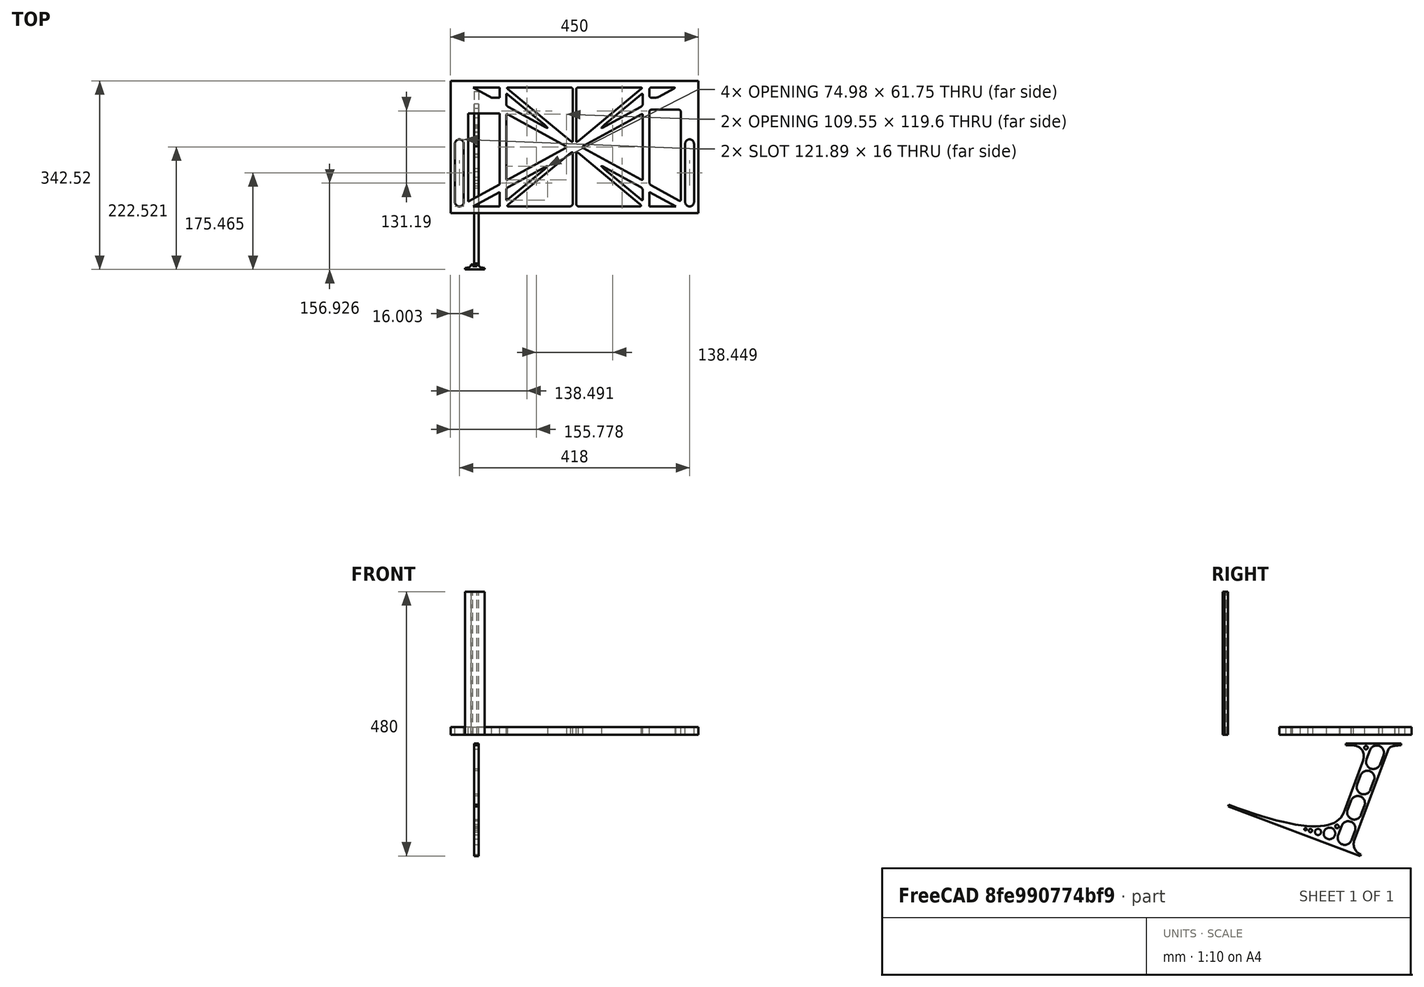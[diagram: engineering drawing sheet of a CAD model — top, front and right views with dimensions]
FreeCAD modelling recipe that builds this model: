
FCSTD DOCUMENT  (FreeCAD 0.19R0.19.2)
Label: laptopStand108
License: All rights reserved
LicenseURL: http://en.wikipedia.org/wiki/All_rights_reserved
objects: Sketcher::SketchObject×3, Part::Extrusion×3
note: 6 computed .brp shape members not serialized (recipe doc carries the construction recipe); baked Part::Feature solids carry a one-line shape summary decoded from their .brp

FEATURE [Sketcher::SketchObject] Sketch
  FullyConstrained = false
  sketch-geometry (298):
    g0: LineSegment StartX=-10.9272 StartY=-82.7794 StartZ=0 EndX=46.0728 EndY=-51.4823 EndZ=0
    g1: LineSegment StartX=366.073 StartY=-91.7794 StartZ=0 EndX=318.073 EndY=-65.424 EndZ=0
    g2: LineSegment StartX=-10.9272 StartY=77.3346 StartZ=0 EndX=-10.9272 EndY=-82.7794 EndZ=0
    g3: LineSegment StartX=-1.92719 StartY=-91.7794 StartZ=0 EndX=46.0728 EndY=-91.7794 EndZ=0
    g4: LineSegment StartX=318.073 StartY=-65.424 StartZ=0 EndX=318.073 EndY=-91.7794 EndZ=0
    g5: LineSegment StartX=318.073 StartY=-91.7794 StartZ=0 EndX=366.073 EndY=-91.7794 EndZ=0
    g6: LineSegment StartX=46.0728 StartY=-65.424 StartZ=0 EndX=-1.92719 EndY=-91.7794 EndZ=0
    g7: LineSegment StartX=46.0728 StartY=-65.424 StartZ=0 EndX=46.0728 EndY=-91.7794 EndZ=0
    g8: LineSegment StartX=46.0728 StartY=77.3346 StartZ=0 EndX=46.0728 EndY=-51.4823 EndZ=0
    g9: LineSegment StartX=-42.9272 StartY=136.221 StartZ=0 EndX=-42.9272 EndY=-103.779 EndZ=0
    g10: LineSegment StartX=407.073 StartY=136.221 StartZ=0 EndX=407.073 EndY=-103.779 EndZ=0
    g11: ArcOfCircle CenterX=-26.9272 CenterY=22.1087 CenterZ=0 NormalX=0 NormalY=0 NormalZ=1 AngleXU=0 Radius=8 StartAngle=1e-16 EndAngle=3.14159
    g12: ArcOfCircle CenterX=-26.9272 CenterY=-83.7794 CenterZ=0 NormalX=0 NormalY=0 NormalZ=1 AngleXU=0 Radius=8 StartAngle=3.14159 EndAngle=6.28319
    g13: LineSegment StartX=-34.9272 StartY=22.1087 StartZ=0 EndX=-34.9272 EndY=-83.7794 EndZ=0
    g14: LineSegment StartX=-18.9272 StartY=22.1087 StartZ=0 EndX=-18.9272 EndY=-83.7794 EndZ=0
    g15: ArcOfCircle CenterX=391.073 CenterY=22.1087 CenterZ=0 NormalX=0 NormalY=0 NormalZ=1 AngleXU=0 Radius=8 StartAngle=-4.4e-15 EndAngle=3.14159
    g16: LineSegment StartX=399.073 StartY=22.1087 StartZ=0 EndX=399.073 EndY=-83.7794 EndZ=0
    g17: LineSegment StartX=383.073 StartY=22.1087 StartZ=0 EndX=383.073 EndY=-83.7794 EndZ=0
    g18: ArcOfCircle CenterX=391.073 CenterY=-83.7794 CenterZ=0 NormalX=0 NormalY=0 NormalZ=1 AngleXU=0 Radius=8 StartAngle=3.14159 EndAngle=6.28319
    g19: Circle CenterX=175.022 CenterY=27.0628 CenterZ=0 NormalX=0 NormalY=0 NormalZ=1 AngleXU=0 Radius=1
    g20: Circle CenterX=179.022 CenterY=24.8665 CenterZ=0 NormalX=0 NormalY=0 NormalZ=1 AngleXU=0 Radius=1
    g21: Circle CenterX=179.022 CenterY=27.0628 CenterZ=0 NormalX=0 NormalY=0 NormalZ=1 AngleXU=0 Radius=1
    g22: BSplineCurve PolesCount=3 KnotsCount=2 Degree=2 IsPeriodic=0
    g23: GeomPoint X=175.022 Y=27.0628 Z=0
    g24: GeomPoint X=179.022 Y=27.0628 Z=0
    g25: Circle CenterX=189.124 CenterY=27.0628 CenterZ=0 NormalX=0 NormalY=0 NormalZ=1 AngleXU=0 Radius=1
    g26: Circle CenterX=185.124 CenterY=24.8665 CenterZ=0 NormalX=0 NormalY=0 NormalZ=1 AngleXU=0 Radius=1
    g27: Circle CenterX=185.124 CenterY=27.0628 CenterZ=0 NormalX=0 NormalY=0 NormalZ=1 AngleXU=0 Radius=1
    g28: BSplineCurve PolesCount=3 KnotsCount=2 Degree=2 IsPeriodic=0
    g29: GeomPoint X=189.124 Y=27.0628 Z=0
    g30: GeomPoint X=185.124 Y=27.0628 Z=0
    g31: Circle CenterX=175.022 CenterY=5.37834 CenterZ=0 NormalX=0 NormalY=0 NormalZ=1 AngleXU=0 Radius=1
    g32: Circle CenterX=179.022 CenterY=7.57463 CenterZ=0 NormalX=0 NormalY=0 NormalZ=1 AngleXU=0 Radius=1
    g33: Circle CenterX=179.022 CenterY=5.34704 CenterZ=0 NormalX=0 NormalY=0 NormalZ=1 AngleXU=0 Radius=1
    g34: BSplineCurve PolesCount=3 KnotsCount=2 Degree=2 IsPeriodic=0
    g35: GeomPoint X=175.022 Y=5.37834 Z=0
    g36: GeomPoint X=179.022 Y=5.34704 Z=0
    g37: Circle CenterX=189.124 CenterY=5.37834 CenterZ=0 NormalX=0 NormalY=0 NormalZ=1 AngleXU=0 Radius=1
    g38: Circle CenterX=185.124 CenterY=7.57463 CenterZ=0 NormalX=0 NormalY=0 NormalZ=1 AngleXU=0 Radius=1
    g39: Circle CenterX=185.124 CenterY=5.34704 CenterZ=0 NormalX=0 NormalY=0 NormalZ=1 AngleXU=0 Radius=1
    g40: BSplineCurve PolesCount=3 KnotsCount=2 Degree=2 IsPeriodic=0
    g41: GeomPoint X=189.124 Y=5.37834 Z=0
    g42: GeomPoint X=185.124 Y=5.34704 Z=0
    g43: Circle CenterX=165.871 CenterY=18.1458 CenterZ=0 NormalX=0 NormalY=0 NormalZ=1 AngleXU=0 Radius=1
    g44: Circle CenterX=169.377 CenterY=16.2206 CenterZ=0 NormalX=0 NormalY=0 NormalZ=1 AngleXU=0 Radius=1
    g45: Circle CenterX=165.871 CenterY=14.2954 CenterZ=0 NormalX=0 NormalY=0 NormalZ=1 AngleXU=0 Radius=1
    g46: BSplineCurve PolesCount=3 KnotsCount=2 Degree=2 IsPeriodic=0
    g47: GeomPoint X=165.871 Y=18.1458 Z=0
    g48: GeomPoint X=165.871 Y=14.2954 Z=0
    g49: Circle CenterX=198.275 CenterY=18.1458 CenterZ=0 NormalX=0 NormalY=0 NormalZ=1 AngleXU=0 Radius=1
    g50: Circle CenterX=194.768 CenterY=16.2206 CenterZ=0 NormalX=0 NormalY=0 NormalZ=1 AngleXU=0 Radius=1
    g51: Circle CenterX=198.275 CenterY=14.2954 CenterZ=0 NormalX=0 NormalY=0 NormalZ=1 AngleXU=0 Radius=1
    g52: BSplineCurve PolesCount=3 KnotsCount=2 Degree=2 IsPeriodic=0
    g53: GeomPoint X=198.275 Y=18.1458 Z=0
    g54: GeomPoint X=198.275 Y=14.2954 Z=0
    g55: LineSegment StartX=407.073 StartY=-103.779 StartZ=0 EndX=-42.9272 EndY=-103.779 EndZ=0
    g56: LineSegment StartX=407.073 StartY=136.221 StartZ=0 EndX=-42.9272 EndY=136.221 EndZ=0
    g57: LineSegment StartX=46.0728 StartY=77.3346 StartZ=0 EndX=-10.9272 EndY=77.3346 EndZ=0
    g58: LineSegment StartX=46.0728 StartY=105.865 StartZ=0 EndX=31.5028 EndY=105.865 EndZ=0
    g59: LineSegment StartX=46.0728 StartY=124.221 StartZ=0 EndX=46.0728 EndY=105.865 EndZ=0
    g60: LineSegment StartX=-1.92719 StartY=124.221 StartZ=0 EndX=31.5028 EndY=105.865 EndZ=0
    g61: LineSegment StartX=46.0728 StartY=124.221 StartZ=0 EndX=-1.92719 EndY=124.221 EndZ=0
    g62: Circle CenterX=125.607 CenterY=54.1951 CenterZ=0 NormalX=0 NormalY=0 NormalZ=1 AngleXU=0 Radius=1
    g63: Circle CenterX=139.632 CenterY=46.4944 CenterZ=0 NormalX=0 NormalY=0 NormalZ=1 AngleXU=0 Radius=1
    g64: Circle CenterX=127.326 CenterY=56.7187 CenterZ=0 NormalX=0 NormalY=0 NormalZ=1 AngleXU=0 Radius=1
    g65: BSplineCurve PolesCount=3 KnotsCount=2 Degree=2 IsPeriodic=0
    g66: GeomPoint X=125.607 Y=54.1951 Z=0
    g67: GeomPoint X=127.326 Y=56.7187 Z=0
    g68: Circle CenterX=236.821 CenterY=56.7187 CenterZ=0 NormalX=0 NormalY=0 NormalZ=1 AngleXU=0 Radius=1
    g69: Circle CenterX=224.513 CenterY=46.4944 CenterZ=0 NormalX=0 NormalY=0 NormalZ=1 AngleXU=0 Radius=1
    g70: Circle CenterX=238.538 CenterY=54.1951 CenterZ=0 NormalX=0 NormalY=0 NormalZ=1 AngleXU=0 Radius=1
    g71: BSplineCurve PolesCount=3 KnotsCount=2 Degree=2 IsPeriodic=0
    g72: GeomPoint X=236.821 Y=56.7187 Z=0
    g73: GeomPoint X=238.538 Y=54.1951 Z=0
    g74: Circle CenterX=238.538 CenterY=-21.7539 CenterZ=0 NormalX=0 NormalY=0 NormalZ=1 AngleXU=0 Radius=1
    g75: Circle CenterX=224.513 CenterY=-14.0532 CenterZ=0 NormalX=0 NormalY=0 NormalZ=1 AngleXU=0 Radius=1
    g76: Circle CenterX=236.821 CenterY=-24.2775 CenterZ=0 NormalX=0 NormalY=0 NormalZ=1 AngleXU=0 Radius=1
    g77: BSplineCurve PolesCount=3 KnotsCount=2 Degree=2 IsPeriodic=0
    g78: GeomPoint X=238.538 Y=-21.7539 Z=0
    g79: GeomPoint X=236.821 Y=-24.2775 Z=0
    g80: Circle CenterX=125.607 CenterY=-21.7539 CenterZ=0 NormalX=0 NormalY=0 NormalZ=1 AngleXU=0 Radius=1
    g81: Circle CenterX=139.632 CenterY=-14.0532 CenterZ=0 NormalX=0 NormalY=0 NormalZ=1 AngleXU=0 Radius=1
    g82: Circle CenterX=127.325 CenterY=-24.2775 CenterZ=0 NormalX=0 NormalY=0 NormalZ=1 AngleXU=0 Radius=1
    g83: BSplineCurve PolesCount=3 KnotsCount=2 Degree=2 IsPeriodic=0
    g84: GeomPoint X=125.607 Y=-21.7539 Z=0
    g85: GeomPoint X=127.325 Y=-24.2775 Z=0
    g86: Circle CenterX=302.996 CenterY=111.695 CenterZ=0 NormalX=0 NormalY=0 NormalZ=1 AngleXU=0 Radius=1
    g87: Circle CenterX=306.073 CenterY=114.251 CenterZ=0 NormalX=0 NormalY=0 NormalZ=1 AngleXU=0 Radius=1
    g88: Circle CenterX=306.073 CenterY=110.251 CenterZ=0 NormalX=0 NormalY=0 NormalZ=1 AngleXU=0 Radius=1
    g89: BSplineCurve PolesCount=3 KnotsCount=2 Degree=2 IsPeriodic=0
    g90: GeomPoint X=302.996 Y=111.695 Z=0
    g91: GeomPoint X=306.073 Y=110.251 Z=0
    g92: Circle CenterX=306.073 CenterY=95.2763 CenterZ=0 NormalX=0 NormalY=0 NormalZ=1 AngleXU=0 Radius=1
    g93: Circle CenterX=306.073 CenterY=91.2763 CenterZ=0 NormalX=0 NormalY=0 NormalZ=1 AngleXU=0 Radius=1
    g94: Circle CenterX=302.567 CenterY=89.3511 CenterZ=0 NormalX=0 NormalY=0 NormalZ=1 AngleXU=0 Radius=1
    g95: BSplineCurve PolesCount=3 KnotsCount=2 Degree=2 IsPeriodic=0
    g96: GeomPoint X=306.073 Y=95.2763 Z=0
    g97: GeomPoint X=302.567 Y=89.3511 Z=0
    g98: LineSegment StartX=306.073 StartY=110.251 StartZ=0 EndX=306.073 EndY=95.2763 EndZ=0
    g99: LineSegment StartX=302.996 StartY=111.695 StartZ=0 EndX=236.821 EndY=56.7187 EndZ=0
    g100: LineSegment StartX=238.538 StartY=54.1951 StartZ=0 EndX=302.567 EndY=89.3511 EndZ=0
    g101: Circle CenterX=61.1496 CenterY=111.695 CenterZ=0 NormalX=0 NormalY=0 NormalZ=1 AngleXU=0 Radius=1
    g102: Circle CenterX=58.0728 CenterY=114.251 CenterZ=0 NormalX=0 NormalY=0 NormalZ=1 AngleXU=0 Radius=1
    g103: Circle CenterX=58.0728 CenterY=110.251 CenterZ=0 NormalX=0 NormalY=0 NormalZ=1 AngleXU=0 Radius=1
    g104: BSplineCurve PolesCount=3 KnotsCount=2 Degree=2 IsPeriodic=0
    g105: GeomPoint X=61.1496 Y=111.695 Z=0
    g106: GeomPoint X=58.0728 Y=110.251 Z=0
    g107: Circle CenterX=61.5791 CenterY=89.3511 CenterZ=0 NormalX=0 NormalY=0 NormalZ=1 AngleXU=0 Radius=1
    g108: Circle CenterX=58.0728 CenterY=91.2763 CenterZ=0 NormalX=0 NormalY=0 NormalZ=1 AngleXU=0 Radius=1
    g109: Circle CenterX=58.0728 CenterY=95.2763 CenterZ=0 NormalX=0 NormalY=0 NormalZ=1 AngleXU=0 Radius=1
    g110: BSplineCurve PolesCount=3 KnotsCount=2 Degree=2 IsPeriodic=0
    g111: GeomPoint X=61.5791 Y=89.3511 Z=0
    g112: GeomPoint X=58.0728 Y=95.2763 Z=0
    g113: LineSegment StartX=58.0728 StartY=110.251 StartZ=0 EndX=58.0728 EndY=95.2763 EndZ=0
    g114: LineSegment StartX=61.1496 StartY=111.695 StartZ=0 EndX=127.326 EndY=56.7187 EndZ=0
    g115: LineSegment StartX=125.607 StartY=54.1951 StartZ=0 EndX=61.5791 EndY=89.3511 EndZ=0
    g116: Circle CenterX=61.5791 CenterY=-56.9099 CenterZ=0 NormalX=0 NormalY=0 NormalZ=1 AngleXU=0 Radius=1
    g117: Circle CenterX=58.0728 CenterY=-58.8351 CenterZ=0 NormalX=0 NormalY=0 NormalZ=1 AngleXU=0 Radius=1
    g118: Circle CenterX=58.0728 CenterY=-62.8351 CenterZ=0 NormalX=0 NormalY=0 NormalZ=1 AngleXU=0 Radius=1
    g119: BSplineCurve PolesCount=3 KnotsCount=2 Degree=2 IsPeriodic=0
    g120: GeomPoint X=61.5791 Y=-56.9099 Z=0
    g121: GeomPoint X=58.0728 Y=-62.8351 Z=0
    g122: Circle CenterX=58.0728 CenterY=-77.8102 CenterZ=0 NormalX=0 NormalY=0 NormalZ=1 AngleXU=0 Radius=1
    g123: Circle CenterX=58.0728 CenterY=-81.8102 CenterZ=0 NormalX=0 NormalY=0 NormalZ=1 AngleXU=0 Radius=1
    g124: Circle CenterX=61.1496 CenterY=-79.2541 CenterZ=0 NormalX=0 NormalY=0 NormalZ=1 AngleXU=0 Radius=1
    g125: BSplineCurve PolesCount=3 KnotsCount=2 Degree=2 IsPeriodic=0
    g126: GeomPoint X=58.0728 Y=-77.8102 Z=0
    g127: GeomPoint X=61.1496 Y=-79.2541 Z=0
    g128: LineSegment StartX=58.0728 StartY=-62.8351 StartZ=0 EndX=58.0728 EndY=-77.8102 EndZ=0
    g129: LineSegment StartX=61.1496 StartY=-79.2541 StartZ=0 EndX=127.325 EndY=-24.2775 EndZ=0
    g130: LineSegment StartX=125.607 StartY=-21.7539 StartZ=0 EndX=61.5791 EndY=-56.9099 EndZ=0
    g131: Circle CenterX=302.567 CenterY=-56.9099 CenterZ=0 NormalX=0 NormalY=0 NormalZ=1 AngleXU=0 Radius=1
    g132: Circle CenterX=306.073 CenterY=-58.8351 CenterZ=0 NormalX=0 NormalY=0 NormalZ=1 AngleXU=0 Radius=1
    g133: Circle CenterX=306.073 CenterY=-62.8351 CenterZ=0 NormalX=0 NormalY=0 NormalZ=1 AngleXU=0 Radius=1
    g134: BSplineCurve PolesCount=3 KnotsCount=2 Degree=2 IsPeriodic=0
    g135: GeomPoint X=302.567 Y=-56.9099 Z=0
    g136: GeomPoint X=306.073 Y=-62.8351 Z=0
    g137: Circle CenterX=302.996 CenterY=-79.2541 CenterZ=0 NormalX=0 NormalY=0 NormalZ=1 AngleXU=0 Radius=1
    g138: Circle CenterX=306.073 CenterY=-81.8102 CenterZ=0 NormalX=0 NormalY=0 NormalZ=1 AngleXU=0 Radius=1
    g139: Circle CenterX=306.073 CenterY=-77.8102 CenterZ=0 NormalX=0 NormalY=0 NormalZ=1 AngleXU=0 Radius=1
    g140: BSplineCurve PolesCount=3 KnotsCount=2 Degree=2 IsPeriodic=0
    g141: GeomPoint X=302.996 Y=-79.2541 Z=0
    g142: GeomPoint X=306.073 Y=-77.8102 Z=0
    g143: LineSegment StartX=306.073 StartY=-62.8351 StartZ=0 EndX=306.073 EndY=-77.8102 EndZ=0
    g144: LineSegment StartX=302.996 StartY=-79.2541 StartZ=0 EndX=236.821 EndY=-24.2775 EndZ=0
    g145: LineSegment StartX=238.538 StartY=-21.7539 StartZ=0 EndX=302.567 EndY=-56.9099 EndZ=0
    g146: Circle CenterX=61.6457 CenterY=-88.8112 CenterZ=0 NormalX=0 NormalY=0 NormalZ=1 AngleXU=0 Radius=1
    g147: Circle CenterX=58.0728 CenterY=-91.7794 CenterZ=0 NormalX=0 NormalY=0 NormalZ=1 AngleXU=0 Radius=1
    g148: Circle CenterX=63.9135 CenterY=-91.7794 CenterZ=0 NormalX=0 NormalY=0 NormalZ=1 AngleXU=0 Radius=1
    g149: BSplineCurve PolesCount=3 KnotsCount=2 Degree=2 IsPeriodic=0
    g150: GeomPoint X=61.6457 Y=-88.8112 Z=0
    g151: GeomPoint X=63.9135 Y=-91.7794 Z=0
    g152: Circle CenterX=179.022 CenterY=-85.8163 CenterZ=0 NormalX=0 NormalY=0 NormalZ=1 AngleXU=0 Radius=1
    g153: Circle CenterX=179.022 CenterY=-91.7794 CenterZ=0 NormalX=0 NormalY=0 NormalZ=1 AngleXU=0 Radius=1
    g154: Circle CenterX=171.895 CenterY=-91.7794 CenterZ=0 NormalX=0 NormalY=0 NormalZ=1 AngleXU=0 Radius=1
    g155: BSplineCurve PolesCount=3 KnotsCount=2 Degree=2 IsPeriodic=0
    g156: GeomPoint X=179.022 Y=-85.8163 Z=0
    g157: GeomPoint X=171.895 Y=-91.7794 Z=0
    g158: Circle CenterX=185.124 CenterY=-86.2028 CenterZ=0 NormalX=0 NormalY=0 NormalZ=1 AngleXU=0 Radius=1
    g159: Circle CenterX=185.124 CenterY=-91.7794 CenterZ=0 NormalX=0 NormalY=0 NormalZ=1 AngleXU=0 Radius=1
    g160: Circle CenterX=191.747 CenterY=-91.7794 CenterZ=0 NormalX=0 NormalY=0 NormalZ=1 AngleXU=0 Radius=1
    g161: BSplineCurve PolesCount=3 KnotsCount=2 Degree=2 IsPeriodic=0
    g162: GeomPoint X=185.124 Y=-86.2028 Z=0
    g163: GeomPoint X=191.747 Y=-91.7794 Z=0
    g164: Circle CenterX=299.888 CenterY=-86.6413 CenterZ=0 NormalX=0 NormalY=0 NormalZ=1 AngleXU=0 Radius=1
    g165: Circle CenterX=306.073 CenterY=-91.7794 CenterZ=0 NormalX=0 NormalY=0 NormalZ=1 AngleXU=0 Radius=1
    g166: Circle CenterX=298.776 CenterY=-91.7794 CenterZ=0 NormalX=0 NormalY=0 NormalZ=1 AngleXU=0 Radius=1
    g167: BSplineCurve PolesCount=3 KnotsCount=2 Degree=2 IsPeriodic=0
    g168: GeomPoint X=299.888 Y=-86.6413 Z=0
    g169: GeomPoint X=298.776 Y=-91.7794 Z=0
    g170: LineSegment StartX=189.124 StartY=5.37834 StartZ=0 EndX=299.888 EndY=-86.6413 EndZ=0
    g171: LineSegment StartX=298.776 StartY=-91.7794 StartZ=0 EndX=191.747 EndY=-91.7794 EndZ=0
    g172: LineSegment StartX=185.124 StartY=-86.2028 StartZ=0 EndX=185.124 EndY=5.34704 EndZ=0
    g173: LineSegment StartX=179.022 StartY=5.34704 StartZ=0 EndX=179.022 EndY=-85.8163 EndZ=0
    g174: LineSegment StartX=171.895 StartY=-91.7794 StartZ=0 EndX=63.9135 EndY=-91.7794 EndZ=0
    g175: LineSegment StartX=61.6457 StartY=-88.8112 StartZ=0 EndX=175.022 EndY=5.37834 EndZ=0
    g176: Circle CenterX=302.073 CenterY=124.221 CenterZ=0 NormalX=0 NormalY=0 NormalZ=1 AngleXU=0 Radius=1
    g177: Circle CenterX=306.073 CenterY=124.221 CenterZ=0 NormalX=0 NormalY=0 NormalZ=1 AngleXU=0 Radius=1
    g178: Circle CenterX=302.996 CenterY=121.665 CenterZ=0 NormalX=0 NormalY=0 NormalZ=1 AngleXU=0 Radius=1
    g179: BSplineCurve PolesCount=3 KnotsCount=2 Degree=2 IsPeriodic=0
    g180: GeomPoint X=302.073 Y=124.221 Z=0
    g181: GeomPoint X=302.996 Y=121.665 Z=0
    g182: Circle CenterX=189.124 CenterY=124.221 CenterZ=0 NormalX=0 NormalY=0 NormalZ=1 AngleXU=0 Radius=1
    g183: Circle CenterX=185.124 CenterY=124.221 CenterZ=0 NormalX=0 NormalY=0 NormalZ=1 AngleXU=0 Radius=1
    g184: Circle CenterX=185.124 CenterY=120.221 CenterZ=0 NormalX=0 NormalY=0 NormalZ=1 AngleXU=0 Radius=1
    g185: BSplineCurve PolesCount=3 KnotsCount=2 Degree=2 IsPeriodic=0
    g186: GeomPoint X=189.124 Y=124.221 Z=0
    g187: GeomPoint X=185.124 Y=120.221 Z=0
    g188: Circle CenterX=175.022 CenterY=124.221 CenterZ=0 NormalX=0 NormalY=0 NormalZ=1 AngleXU=0 Radius=1
    g189: Circle CenterX=179.022 CenterY=124.221 CenterZ=0 NormalX=0 NormalY=0 NormalZ=1 AngleXU=0 Radius=1
    g190: Circle CenterX=179.022 CenterY=120.221 CenterZ=0 NormalX=0 NormalY=0 NormalZ=1 AngleXU=0 Radius=1
    g191: BSplineCurve PolesCount=3 KnotsCount=2 Degree=2 IsPeriodic=0
    g192: GeomPoint X=175.022 Y=124.221 Z=0
    g193: GeomPoint X=179.022 Y=120.221 Z=0
    g194: Circle CenterX=62.0728 CenterY=124.221 CenterZ=0 NormalX=0 NormalY=0 NormalZ=1 AngleXU=0 Radius=1
    g195: Circle CenterX=58.0728 CenterY=124.221 CenterZ=0 NormalX=0 NormalY=0 NormalZ=1 AngleXU=0 Radius=1
    g196: Circle CenterX=61.1496 CenterY=121.665 CenterZ=0 NormalX=0 NormalY=0 NormalZ=1 AngleXU=0 Radius=1
    g197: BSplineCurve PolesCount=3 KnotsCount=2 Degree=2 IsPeriodic=0
    g198: GeomPoint X=62.0728 Y=124.221 Z=0
    g199: GeomPoint X=61.1496 Y=121.665 Z=0
    g200: LineSegment StartX=62.0728 StartY=124.221 StartZ=0 EndX=175.022 EndY=124.221 EndZ=0
    g201: LineSegment StartX=179.022 StartY=120.221 StartZ=0 EndX=179.022 EndY=27.0628 EndZ=0
    g202: LineSegment StartX=185.124 StartY=27.0628 StartZ=0 EndX=185.124 EndY=120.221 EndZ=0
    g203: LineSegment StartX=189.124 StartY=124.221 StartZ=0 EndX=302.073 EndY=124.221 EndZ=0
    g204: LineSegment StartX=302.996 StartY=121.665 StartZ=0 EndX=189.124 EndY=27.0628 EndZ=0
    g205: LineSegment StartX=175.022 StartY=27.0628 StartZ=0 EndX=61.1496 EndY=121.665 EndZ=0
    g206: Circle CenterX=61.5791 CenterY=75.4095 CenterZ=0 NormalX=0 NormalY=0 NormalZ=1 AngleXU=0 Radius=1
    g207: Circle CenterX=58.0728 CenterY=77.3346 CenterZ=0 NormalX=0 NormalY=0 NormalZ=1 AngleXU=0 Radius=1
    g208: Circle CenterX=58.0728 CenterY=73.3346 CenterZ=0 NormalX=0 NormalY=0 NormalZ=1 AngleXU=0 Radius=1
    g209: BSplineCurve PolesCount=3 KnotsCount=2 Degree=2 IsPeriodic=0
    g210: GeomPoint X=61.5791 Y=75.4095 Z=0
    g211: GeomPoint X=58.0728 Y=73.3346 Z=0
    g212: Circle CenterX=58.0728 CenterY=-40.8935 CenterZ=0 NormalX=0 NormalY=0 NormalZ=1 AngleXU=0 Radius=1
    g213: Circle CenterX=58.0728 CenterY=-44.8935 CenterZ=0 NormalX=0 NormalY=0 NormalZ=1 AngleXU=0 Radius=1
    g214: Circle CenterX=61.5791 CenterY=-42.9683 CenterZ=0 NormalX=0 NormalY=0 NormalZ=1 AngleXU=0 Radius=1
    g215: BSplineCurve PolesCount=3 KnotsCount=2 Degree=2 IsPeriodic=0
    g216: GeomPoint X=58.0728 Y=-40.8935 Z=0
    g217: GeomPoint X=61.5791 Y=-42.9683 Z=0
    g218: LineSegment StartX=61.5791 StartY=-42.9683 StartZ=0 EndX=165.871 EndY=14.2954 EndZ=0
    g219: LineSegment StartX=165.871 StartY=18.1458 StartZ=0 EndX=61.5791 EndY=75.4095 EndZ=0
    g220: LineSegment StartX=58.0728 StartY=73.3346 StartZ=0 EndX=58.0728 EndY=-40.8935 EndZ=0
    g221: Circle CenterX=302.567 CenterY=-42.9683 CenterZ=0 NormalX=0 NormalY=0 NormalZ=1 AngleXU=0 Radius=1
    g222: Circle CenterX=306.073 CenterY=-44.8935 CenterZ=0 NormalX=0 NormalY=0 NormalZ=1 AngleXU=0 Radius=1
    g223: Circle CenterX=306.073 CenterY=-40.8935 CenterZ=0 NormalX=0 NormalY=0 NormalZ=1 AngleXU=0 Radius=1
    g224: BSplineCurve PolesCount=3 KnotsCount=2 Degree=2 IsPeriodic=0
    g225: GeomPoint X=302.567 Y=-42.9683 Z=0
    g226: GeomPoint X=306.073 Y=-40.8935 Z=0
    g227: Circle CenterX=306.073 CenterY=73.3346 CenterZ=0 NormalX=0 NormalY=0 NormalZ=1 AngleXU=0 Radius=1
    g228: Circle CenterX=306.073 CenterY=77.3346 CenterZ=0 NormalX=0 NormalY=0 NormalZ=1 AngleXU=0 Radius=1
    g229: Circle CenterX=302.567 CenterY=75.4095 CenterZ=0 NormalX=0 NormalY=0 NormalZ=1 AngleXU=0 Radius=1
    g230: BSplineCurve PolesCount=3 KnotsCount=2 Degree=2 IsPeriodic=0
    g231: GeomPoint X=306.073 Y=73.3346 Z=0
    g232: GeomPoint X=302.567 Y=75.4095 Z=0
    g233: LineSegment StartX=302.567 StartY=-42.9683 StartZ=0 EndX=198.275 EndY=14.2954 EndZ=0
    g234: LineSegment StartX=198.275 StartY=18.1458 StartZ=0 EndX=302.567 EndY=75.4095 EndZ=0
    g235: LineSegment StartX=306.073 StartY=73.3346 StartZ=0 EndX=306.073 EndY=-40.8935 EndZ=0
    g236: LineSegment StartX=322.073 StartY=105.865 StartZ=0 EndX=328.643 EndY=105.865 EndZ=0
    g237: LineSegment StartX=318.073 StartY=120.221 StartZ=0 EndX=318.073 EndY=109.865 EndZ=0
    g238: LineSegment StartX=336.157 StartY=107.779 StartZ=0 EndX=362.567 EndY=122.294 EndZ=0
    g239: Circle CenterX=362.073 CenterY=124.221 CenterZ=0 NormalX=0 NormalY=0 NormalZ=1 AngleXU=0 Radius=1
    g240: Circle CenterX=366.073 CenterY=124.221 CenterZ=0 NormalX=0 NormalY=0 NormalZ=1 AngleXU=0 Radius=1
    g241: Circle CenterX=362.567 CenterY=122.294 CenterZ=0 NormalX=0 NormalY=0 NormalZ=1 AngleXU=0 Radius=1
    g242: BSplineCurve PolesCount=3 KnotsCount=2 Degree=2 IsPeriodic=0
    g243: GeomPoint X=362.073 Y=124.221 Z=0
    g244: GeomPoint X=362.567 Y=122.294 Z=0
    g245: Circle CenterX=322.073 CenterY=124.221 CenterZ=0 NormalX=0 NormalY=0 NormalZ=1 AngleXU=0 Radius=1
    g246: Circle CenterX=318.073 CenterY=124.221 CenterZ=0 NormalX=0 NormalY=0 NormalZ=1 AngleXU=0 Radius=1
    g247: Circle CenterX=318.073 CenterY=120.221 CenterZ=0 NormalX=0 NormalY=0 NormalZ=1 AngleXU=0 Radius=1
    g248: BSplineCurve PolesCount=3 KnotsCount=2 Degree=2 IsPeriodic=0
    g249: GeomPoint X=322.073 Y=124.221 Z=0
    g250: GeomPoint X=318.073 Y=120.221 Z=0
    g251: Circle CenterX=322.073 CenterY=105.865 CenterZ=0 NormalX=0 NormalY=0 NormalZ=1 AngleXU=0 Radius=1
    g252: Circle CenterX=318.073 CenterY=105.865 CenterZ=0 NormalX=0 NormalY=0 NormalZ=1 AngleXU=0 Radius=1
    g253: Circle CenterX=318.073 CenterY=109.865 CenterZ=0 NormalX=0 NormalY=0 NormalZ=1 AngleXU=0 Radius=1
    g254: BSplineCurve PolesCount=3 KnotsCount=2 Degree=2 IsPeriodic=0
    g255: GeomPoint X=322.073 Y=105.865 Z=0
    g256: GeomPoint X=318.073 Y=109.865 Z=0
    g257: Circle CenterX=336.157 CenterY=107.779 CenterZ=0 NormalX=0 NormalY=0 NormalZ=1 AngleXU=0 Radius=1
    g258: Circle CenterX=332.651 CenterY=105.853 CenterZ=0 NormalX=0 NormalY=0 NormalZ=1 AngleXU=0 Radius=1
    g259: Circle CenterX=328.643 CenterY=105.865 CenterZ=0 NormalX=0 NormalY=0 NormalZ=1 AngleXU=0 Radius=1
    g260: BSplineCurve PolesCount=3 KnotsCount=2 Degree=2 IsPeriodic=0
    g261: GeomPoint X=336.157 Y=107.779 Z=0
    g262: GeomPoint X=328.643 Y=105.865 Z=0
    g263: LineSegment StartX=322.073 StartY=124.221 StartZ=0 EndX=362.073 EndY=124.221 EndZ=0
    g264: Circle CenterX=371.567 CenterY=-80.8644 CenterZ=0 NormalX=0 NormalY=0 NormalZ=1 AngleXU=0 Radius=1
    g265: Circle CenterX=375.073 CenterY=-82.7896 CenterZ=0 NormalX=0 NormalY=0 NormalZ=1 AngleXU=0 Radius=1
    g266: Circle CenterX=375.073 CenterY=-78.7896 CenterZ=0 NormalX=0 NormalY=0 NormalZ=1 AngleXU=0 Radius=1
    g267: BSplineCurve PolesCount=3 KnotsCount=2 Degree=2 IsPeriodic=0
    g268: GeomPoint X=371.567 Y=-80.8644 Z=0
    g269: GeomPoint X=375.073 Y=-78.7896 Z=0
    g270: Circle CenterX=321.579 CenterY=-53.4075 CenterZ=0 NormalX=0 NormalY=0 NormalZ=1 AngleXU=0 Radius=1
    g271: Circle CenterX=318.073 CenterY=-51.4823 CenterZ=0 NormalX=0 NormalY=0 NormalZ=1 AngleXU=0 Radius=1
    g272: Circle CenterX=318.073 CenterY=-47.4823 CenterZ=0 NormalX=0 NormalY=0 NormalZ=1 AngleXU=0 Radius=1
    g273: BSplineCurve PolesCount=3 KnotsCount=2 Degree=2 IsPeriodic=0
    g274: GeomPoint X=321.579 Y=-53.4075 Z=0
    g275: GeomPoint X=318.073 Y=-47.4823 Z=0
    g276: Circle CenterX=318.073 CenterY=79.9235 CenterZ=0 NormalX=0 NormalY=0 NormalZ=1 AngleXU=0 Radius=1
    g277: Circle CenterX=318.073 CenterY=83.9235 CenterZ=0 NormalX=0 NormalY=0 NormalZ=1 AngleXU=0 Radius=1
    g278: Circle CenterX=322.073 CenterY=83.9235 CenterZ=0 NormalX=0 NormalY=0 NormalZ=1 AngleXU=0 Radius=1
    g279: BSplineCurve PolesCount=3 KnotsCount=2 Degree=2 IsPeriodic=0
    g280: GeomPoint X=318.073 Y=79.9235 Z=0
    g281: GeomPoint X=322.073 Y=83.9235 Z=0
    g282: Circle CenterX=375.073 CenterY=79.9235 CenterZ=0 NormalX=0 NormalY=0 NormalZ=1 AngleXU=0 Radius=1
    g283: Circle CenterX=375.073 CenterY=83.9235 CenterZ=0 NormalX=0 NormalY=0 NormalZ=1 AngleXU=0 Radius=1
    g284: Circle CenterX=371.073 CenterY=83.9235 CenterZ=0 NormalX=0 NormalY=0 NormalZ=1 AngleXU=0 Radius=1
    g285: BSplineCurve PolesCount=3 KnotsCount=2 Degree=2 IsPeriodic=0
    g286: GeomPoint X=375.073 Y=79.9235 Z=0
    g287: GeomPoint X=371.073 Y=83.9235 Z=0
    g288: LineSegment StartX=322.073 StartY=83.9235 StartZ=0 EndX=371.073 EndY=83.9235 EndZ=0
    g289: LineSegment StartX=375.073 StartY=79.9235 StartZ=0 EndX=375.073 EndY=-78.7896 EndZ=0
    g290: LineSegment StartX=371.567 StartY=-80.8644 StartZ=0 EndX=321.579 EndY=-53.4075 EndZ=0
    g291: LineSegment StartX=318.073 StartY=-47.4823 StartZ=0 EndX=318.073 EndY=79.9235 EndZ=0
    g292: LineSegment StartX=319.639 StartY=-65.1825 StartZ=0 EndX=324.101 EndY=-67.6327 EndZ=0
    g293: LineSegment StartX=366.617 StartY=-91.048 StartZ=0 EndX=360.96 EndY=-87.9419 EndZ=0
    g294: LineSegment StartX=365.563 StartY=-92.7205 StartZ=0 EndX=358.36 EndY=-92.7205 EndZ=0
    g295: LineSegment StartX=318.76 StartY=-92.6854 StartZ=0 EndX=325.717 EndY=-92.6854 EndZ=0
    g296: LineSegment StartX=317.038 StartY=-91.4204 StartZ=0 EndX=317.038 EndY=-87.2391 EndZ=0
    g297: LineSegment StartX=317.566 StartY=-66.1569 StartZ=0 EndX=317.566 EndY=-69.2841 EndZ=0
  constraints (494):
    c: Horizontal(g3)
    c: Coincident(g4,g1)
    c: Coincident(g7,g6)
    c: Coincident(g0,g8)
    c: Block(g1)
    c: Block(g4)
    c: Block(g7)
    c: Block(g6)
    c: Block(g0)
    c: Block(g2)
    c: Block(g5)
    c: Block(g3)
    c: Vertical(g9)
    c: Vertical(g10)
    c: Block(g10)
    c: Block(g9)
    c: Tangent(g11,g14) = 1.5708
    c: Tangent(g11,g13) = -1.5708
    c: Tangent(g13,g12) = -1.5708
    c: Tangent(g14,g12) = 1.5708
    c: Vertical(g13)
    c: Equal(g11,g12)
    c: Block(g14)
    c: Block(g13)
    c: Tangent(g15,g16) = 1.5708
    c: Tangent(g16,g18) = 1.5708
    c: Equal(g15,g18)
    c: Coincident(g17,g15)
    c: Coincident(g17,g18)
    c: Block(g16)
    c: Block(g17)
    c: Weight(g19) = 1
    c: Equal(g19,g20)
    c: Equal(g19,g21)
    c: InternalAlignment(g19,g22)
    c: InternalAlignment(g20,g22)
    c: InternalAlignment(g21,g22)
    c: InternalAlignment(g23,g22)
    c: InternalAlignment(g24,g22)
    c: Weight(g25) = 1
    c: Equal(g25,g26)
    c: Equal(g25,g27)
    c: InternalAlignment(g25,g28)
    c: InternalAlignment(g26,g28)
    c: InternalAlignment(g27,g28)
    c: InternalAlignment(g29,g28)
    c: InternalAlignment(g30,g28)
    c: Block(g28)
    c: Block(g22)
    c: Weight(g31) = 1
    c: Equal(g31,g32)
    c: Equal(g31,g33)
    c: InternalAlignment(g31,g34)
    c: InternalAlignment(g32,g34)
    c: InternalAlignment(g33,g34)
    c: InternalAlignment(g35,g34)
    c: InternalAlignment(g36,g34)
    c: Weight(g37) = 1
    c: Equal(g37,g38)
    c: Equal(g37,g39)
    c: InternalAlignment(g37,g40)
    c: InternalAlignment(g38,g40)
    c: InternalAlignment(g39,g40)
    c: InternalAlignment(g41,g40)
    c: InternalAlignment(g42,g40)
    c: Block(g40)
    c: Block(g34)
    c: Weight(g43) = 1
    c: Equal(g43,g44)
    c: Equal(g43,g45)
    c: InternalAlignment(g43,g46)
    c: InternalAlignment(g44,g46)
    c: InternalAlignment(g45,g46)
    c: InternalAlignment(g47,g46)
    c: InternalAlignment(g48,g46)
    c: Weight(g49) = 1
    c: Equal(g49,g50)
    c: Equal(g49,g51)
    c: InternalAlignment(g49,g52)
    c: InternalAlignment(g50,g52)
    c: InternalAlignment(g51,g52)
    c: InternalAlignment(g53,g52)
    c: InternalAlignment(g54,g52)
    c: Block(g46)
    c: Block(g52)
    c: Coincident(g55,g10)
    c: Coincident(g55,g9)
    c: Horizontal(g55)
    c: Distance(g55) = 450
    c: Coincident(g56,g10)
    c: Coincident(g56,g9)
    c: Horizontal(g56)
    c: Horizontal(g57)
    c: Coincident(g8,g57)
    c: Horizontal(g58)
    c: Vertical(g59)
    c: Block(g59)
    c: Block(g58)
    c: Block(g57)
    c: Distance(g59) = 18.3554
    c: Coincident(g61,g59)
    c: Coincident(g61,g60)
    c: Horizontal(g61)
    c: Block(g61)
    c: Block(g60)
    c: Coincident(g58,g60)
    c: Coincident(g2,g57)
    c: Weight(g62) = 1
    c: Equal(g62,g63)
    c: Equal(g62,g64)
    c: InternalAlignment(g62,g65)
    c: InternalAlignment(g63,g65)
    c: InternalAlignment(g64,g65)
    c: InternalAlignment(g66,g65)
    c: InternalAlignment(g67,g65)
    c: Block(g65)
    c: Weight(g68) = 1
    c: Equal(g68,g69)
    c: Equal(g68,g70)
    c: InternalAlignment(g68,g71)
    c: InternalAlignment(g69,g71)
    c: InternalAlignment(g70,g71)
    c: InternalAlignment(g72,g71)
    c: InternalAlignment(g73,g71)
    c: Block(g71)
    c: Weight(g74) = 1
    c: Equal(g74,g75)
    c: Equal(g74,g76)
    c: InternalAlignment(g74,g77)
    c: InternalAlignment(g75,g77)
    c: InternalAlignment(g76,g77)
    c: InternalAlignment(g78,g77)
    c: InternalAlignment(g79,g77)
    c: Block(g77)
    c: Weight(g80) = 1
    c: Equal(g80,g81)
    c: Equal(g80,g82)
    c: InternalAlignment(g80,g83)
    c: InternalAlignment(g81,g83)
    c: InternalAlignment(g82,g83)
    c: InternalAlignment(g84,g83)
    c: InternalAlignment(g85,g83)
    c: Block(g83)
    c: Weight(g86) = 1
    c: Equal(g86,g87)
    c: Equal(g86,g88)
    c: InternalAlignment(g86,g89)
    c: InternalAlignment(g87,g89)
    c: InternalAlignment(g88,g89)
    c: InternalAlignment(g90,g89)
    c: InternalAlignment(g91,g89)
    c: Weight(g92) = 1
    c: Equal(g92,g93)
    c: Equal(g92,g94)
    c: InternalAlignment(g92,g95)
    c: InternalAlignment(g93,g95)
    c: InternalAlignment(g94,g95)
    c: InternalAlignment(g96,g95)
    c: InternalAlignment(g97,g95)
    c: Block(g89)
    c: Block(g95)
    c: Coincident(g98,g89)
    c: Coincident(g98,g95)
    c: Vertical(g98)
    c: Coincident(g99,g89)
    c: Coincident(g99,g71)
    c: Coincident(g100,g71)
    c: Coincident(g100,g95)
    c: Weight(g101) = 1
    c: Equal(g101,g102)
    c: Equal(g101,g103)
    c: InternalAlignment(g101,g104)
    c: InternalAlignment(g102,g104)
    c: InternalAlignment(g103,g104)
    c: InternalAlignment(g105,g104)
    c: InternalAlignment(g106,g104)
    c: Weight(g107) = 1
    c: Equal(g107,g108)
    c: Equal(g107,g109)
    c: InternalAlignment(g107,g110)
    c: InternalAlignment(g108,g110)
    c: InternalAlignment(g109,g110)
    c: InternalAlignment(g111,g110)
    c: InternalAlignment(g112,g110)
    c: Block(g104)
    c: Block(g110)
    c: Coincident(g113,g104)
    c: Coincident(g113,g110)
    c: Vertical(g113)
    c: Coincident(g114,g104)
    c: Coincident(g114,g65)
    c: Coincident(g115,g65)
    c: Coincident(g115,g110)
    c: Weight(g116) = 1
    c: Equal(g116,g117)
    c: Equal(g116,g118)
    c: InternalAlignment(g116,g119)
    c: InternalAlignment(g117,g119)
    c: InternalAlignment(g118,g119)
    c: InternalAlignment(g120,g119)
    c: InternalAlignment(g121,g119)
    c: Weight(g122) = 1
    c: Equal(g122,g123)
    c: Equal(g122,g124)
    c: InternalAlignment(g122,g125)
    c: InternalAlignment(g123,g125)
    c: InternalAlignment(g124,g125)
    c: InternalAlignment(g126,g125)
    c: InternalAlignment(g127,g125)
    c: Block(g119)
    c: Block(g125)
    c: Coincident(g128,g119)
    c: Coincident(g128,g125)
    c: Vertical(g128)
    c: Coincident(g129,g125)
    c: Coincident(g129,g83)
    c: Coincident(g130,g83)
    c: Coincident(g130,g119)
    c: Weight(g131) = 1
    c: Equal(g131,g132)
    c: Equal(g131,g133)
    c: InternalAlignment(g131,g134)
    c: InternalAlignment(g132,g134)
    c: InternalAlignment(g133,g134)
    c: InternalAlignment(g135,g134)
    c: InternalAlignment(g136,g134)
    c: Weight(g137) = 1
    c: Equal(g137,g138)
    c: Equal(g137,g139)
    c: InternalAlignment(g137,g140)
    c: InternalAlignment(g138,g140)
    c: InternalAlignment(g139,g140)
    c: InternalAlignment(g141,g140)
    c: InternalAlignment(g142,g140)
    c: Block(g134)
    c: Block(g140)
    c: Coincident(g143,g134)
    c: Coincident(g143,g140)
    c: Vertical(g143)
    c: Coincident(g144,g140)
    c: Coincident(g144,g77)
    c: Coincident(g145,g77)
    c: Coincident(g145,g134)
    c: Weight(g146) = 1
    c: Equal(g146,g147)
    c: Equal(g146,g148)
    c: InternalAlignment(g146,g149)
    c: InternalAlignment(g147,g149)
    c: InternalAlignment(g148,g149)
    c: InternalAlignment(g150,g149)
    c: InternalAlignment(g151,g149)
    c: Weight(g152) = 1
    c: Equal(g152,g153)
    c: Equal(g152,g154)
    c: InternalAlignment(g152,g155)
    c: InternalAlignment(g153,g155)
    c: InternalAlignment(g154,g155)
    c: InternalAlignment(g156,g155)
    c: InternalAlignment(g157,g155)
    c: Weight(g158) = 1
    c: Equal(g158,g159)
    c: Equal(g158,g160)
    c: InternalAlignment(g158,g161)
    c: InternalAlignment(g159,g161)
    c: InternalAlignment(g160,g161)
    c: InternalAlignment(g162,g161)
    c: InternalAlignment(g163,g161)
    c: Weight(g164) = 1
    c: Equal(g164,g165)
    c: Equal(g164,g166)
    c: InternalAlignment(g164,g167)
    c: InternalAlignment(g165,g167)
    c: InternalAlignment(g166,g167)
    c: InternalAlignment(g168,g167)
    c: InternalAlignment(g169,g167)
    c: Block(g167)
    c: Block(g161)
    c: Block(g155)
    c: Block(g149)
    c: Coincident(g170,g40)
    c: Coincident(g170,g167)
    c: Coincident(g171,g167)
    c: Coincident(g171,g161)
    c: Horizontal(g171)
    c: Coincident(g172,g161)
    c: Coincident(g172,g40)
    c: Vertical(g172)
    c: Coincident(g173,g34)
    c: Coincident(g173,g155)
    c: Vertical(g173)
    c: Coincident(g174,g155)
    c: Coincident(g174,g149)
    c: Horizontal(g174)
    c: Coincident(g175,g149)
    c: Coincident(g175,g34)
    c: Weight(g176) = 1
    c: Equal(g176,g177)
    c: Equal(g176,g178)
    c: InternalAlignment(g176,g179)
    c: InternalAlignment(g177,g179)
    c: InternalAlignment(g178,g179)
    c: InternalAlignment(g180,g179)
    c: InternalAlignment(g181,g179)
    c: Weight(g182) = 1
    c: Equal(g182,g183)
    c: Equal(g182,g184)
    c: InternalAlignment(g182,g185)
    c: InternalAlignment(g183,g185)
    c: InternalAlignment(g184,g185)
    c: InternalAlignment(g186,g185)
    c: InternalAlignment(g187,g185)
    c: Weight(g188) = 1
    c: Equal(g188,g189)
    c: Equal(g188,g190)
    c: InternalAlignment(g188,g191)
    c: InternalAlignment(g189,g191)
    c: InternalAlignment(g190,g191)
    c: InternalAlignment(g192,g191)
    c: InternalAlignment(g193,g191)
    c: Weight(g194) = 1
    c: Equal(g194,g195)
    c: Equal(g194,g196)
    c: InternalAlignment(g194,g197)
    c: InternalAlignment(g195,g197)
    c: InternalAlignment(g196,g197)
    c: InternalAlignment(g198,g197)
    c: InternalAlignment(g199,g197)
    c: Block(g197)
    c: Block(g191)
    c: Block(g185)
    c: Block(g179)
    c: Coincident(g200,g197)
    c: Coincident(g200,g191)
    c: Horizontal(g200)
    c: Coincident(g201,g191)
    c: Coincident(g201,g22)
    c: Vertical(g201)
    c: Coincident(g202,g28)
    c: Coincident(g202,g185)
    c: Vertical(g202)
    c: Coincident(g203,g185)
    c: Coincident(g203,g179)
    c: Horizontal(g203)
    c: Coincident(g204,g179)
    c: Coincident(g204,g28)
    c: Coincident(g205,g22)
    c: Weight(g206) = 1
    c: Equal(g206,g207)
    c: Equal(g206,g208)
    c: InternalAlignment(g206,g209)
    c: InternalAlignment(g207,g209)
    c: InternalAlignment(g208,g209)
    c: InternalAlignment(g210,g209)
    c: InternalAlignment(g211,g209)
    c: Weight(g212) = 1
    c: Equal(g212,g213)
    c: Equal(g212,g214)
    c: InternalAlignment(g212,g215)
    c: InternalAlignment(g213,g215)
    c: InternalAlignment(g214,g215)
    c: InternalAlignment(g216,g215)
    c: InternalAlignment(g217,g215)
    c: Block(g215)
    c: Block(g209)
    c: Coincident(g218,g215)
    c: Coincident(g218,g46)
    c: Coincident(g219,g46)
    c: Coincident(g219,g209)
    c: Coincident(g220,g209)
    c: Coincident(g220,g215)
    c: Vertical(g220)
    c: Weight(g221) = 1
    c: Equal(g221,g222)
    c: Equal(g221,g223)
    c: InternalAlignment(g221,g224)
    c: InternalAlignment(g222,g224)
    c: InternalAlignment(g223,g224)
    c: InternalAlignment(g225,g224)
    c: InternalAlignment(g226,g224)
    c: Weight(g227) = 1
    c: Equal(g227,g228)
    c: Equal(g227,g229)
    c: InternalAlignment(g227,g230)
    c: InternalAlignment(g228,g230)
    c: InternalAlignment(g229,g230)
    c: InternalAlignment(g231,g230)
    c: InternalAlignment(g232,g230)
    c: Block(g230)
    c: Block(g224)
    c: Coincident(g233,g224)
    c: Coincident(g233,g52)
    c: Coincident(g234,g52)
    c: Coincident(g234,g230)
    c: Coincident(g235,g230)
    c: Coincident(g235,g224)
    c: Vertical(g235)
    c: Horizontal(g236)
    c: Block(g236)
    c: Vertical(g237)
    c: Block(g237)
    c: Block(g238)
    c: Weight(g239) = 1
    c: Equal(g239,g240)
    c: Equal(g239,g241)
    c: InternalAlignment(g239,g242)
    c: InternalAlignment(g240,g242)
    c: InternalAlignment(g241,g242)
    c: InternalAlignment(g243,g242)
    c: InternalAlignment(g244,g242)
    c: Weight(g245) = 1
    c: Equal(g245,g246)
    c: Equal(g245,g247)
    c: InternalAlignment(g245,g248)
    c: InternalAlignment(g246,g248)
    c: InternalAlignment(g247,g248)
    c: InternalAlignment(g249,g248)
    c: InternalAlignment(g250,g248)
    c: Weight(g251) = 1
    c: Equal(g251,g252)
    c: Equal(g251,g253)
    c: InternalAlignment(g251,g254)
    c: InternalAlignment(g252,g254)
    c: InternalAlignment(g253,g254)
    c: InternalAlignment(g255,g254)
    c: InternalAlignment(g256,g254)
    c: Weight(g257) = 1
    c: Equal(g257,g258)
    c: Equal(g257,g259)
    c: InternalAlignment(g257,g260)
    c: InternalAlignment(g258,g260)
    c: InternalAlignment(g259,g260)
    c: InternalAlignment(g261,g260)
    c: InternalAlignment(g262,g260)
    c: Block(g242)
    c: Block(g248)
    c: Block(g254)
    c: Block(g260)
    c: Coincident(g263,g248)
    c: Coincident(g263,g242)
    c: Horizontal(g263)
    c: Block(g205)
    c: Weight(g264) = 1
    c: Equal(g264,g265)
    c: Equal(g264,g266)
    c: InternalAlignment(g264,g267)
    c: InternalAlignment(g265,g267)
    c: InternalAlignment(g266,g267)
    c: InternalAlignment(g268,g267)
    c: InternalAlignment(g269,g267)
    c: Weight(g270) = 1
    c: Equal(g270,g271)
    c: Equal(g270,g272)
    c: InternalAlignment(g270,g273)
    c: InternalAlignment(g271,g273)
    c: InternalAlignment(g272,g273)
    c: InternalAlignment(g274,g273)
    c: InternalAlignment(g275,g273)
    c: Weight(g276) = 1
    c: Equal(g276,g277)
    c: Equal(g276,g278)
    c: InternalAlignment(g276,g279)
    c: InternalAlignment(g277,g279)
    c: InternalAlignment(g278,g279)
    c: InternalAlignment(g280,g279)
    c: InternalAlignment(g281,g279)
    c: Weight(g282) = 1
    c: Equal(g282,g283)
    c: Equal(g282,g284)
    c: InternalAlignment(g282,g285)
    c: InternalAlignment(g283,g285)
    c: InternalAlignment(g284,g285)
    c: InternalAlignment(g286,g285)
    c: InternalAlignment(g287,g285)
    c: Block(g267)
    c: Block(g273)
    c: Block(g279)
    c: Block(g285)
    c: Coincident(g288,g279)
    c: Coincident(g288,g285)
    c: Horizontal(g288)
    c: Coincident(g289,g285)
    c: Coincident(g289,g267)
    c: Vertical(g289)
    c: Coincident(g290,g267)
    c: Coincident(g290,g273)
    c: Coincident(g291,g273)
    c: Coincident(g291,g279)
    c: Vertical(g291)
    c: Horizontal(g294)
    c: Horizontal(g295)
    c: Vertical(g296)
    c: Vertical(g297)
    c: Parallel(g292,g1)
    c: Parallel(g293,g1)
FEATURE [Sketcher::SketchObject] Sketch001
  FullyConstrained = true
  MapMode = 4
  Placement = pos=(0,0,0) rot=(0.57735,0.57735,0.57735;2.0944rad)
  Support = -> [Sketch]
  sketch-geometry (46):
    g0: BSplineCurve PolesCount=3 KnotsCount=2 Degree=2 IsPeriodic=0
    g1: ArcOfCircle CenterX=73.1223 CenterY=-32.291 CenterZ=0 NormalX=0 NormalY=0 NormalZ=1 AngleXU=0 Radius=13 StartAngle=5.92268 EndAngle=9.06428
    g2: ArcOfCircle CenterX=66.7816 CenterY=-49.1439 CenterZ=0 NormalX=0 NormalY=0 NormalZ=1 AngleXU=0 Radius=13 StartAngle=2.78068 EndAngle=5.92131
    g3: ArcOfCircle CenterX=55.9263 CenterY=-78.1807 CenterZ=0 NormalX=0 NormalY=0 NormalZ=1 AngleXU=0 Radius=13 StartAngle=5.92268 EndAngle=9.06428
    g4: ArcOfCircle CenterX=49.5884 CenterY=-95.0342 CenterZ=0 NormalX=0 NormalY=0 NormalZ=1 AngleXU=0 Radius=13 StartAngle=2.78068 EndAngle=5.92131
    g5: ArcOfCircle CenterX=38.7206 CenterY=-124.067 CenterZ=0 NormalX=0 NormalY=0 NormalZ=1 AngleXU=0 Radius=13 StartAngle=5.92268 EndAngle=9.06428
    g6: ArcOfCircle CenterX=32.3875 CenterY=-140.92 CenterZ=0 NormalX=0 NormalY=0 NormalZ=1 AngleXU=0 Radius=13 StartAngle=2.78068 EndAngle=5.92131
    g7: ArcOfCircle CenterX=21.4715 CenterY=-169.934 CenterZ=0 NormalX=0 NormalY=0 NormalZ=1 AngleXU=0 Radius=13 StartAngle=5.92268 EndAngle=9.06428
    g8: ArcOfCircle CenterX=15.1336 CenterY=-186.787 CenterZ=0 NormalX=0 NormalY=0 NormalZ=1 AngleXU=0 Radius=13 StartAngle=2.78068 EndAngle=5.92131
    g9-g12: Circle x4 (B-spline internal-alignment scaffolding for g13; pole/knot coordinates omitted)
    g13: BSplineCurve PolesCount=4 KnotsCount=2 Degree=3 IsPeriodic=0
    g14: GeomPoint X=28.8094 Y=-19.0875 Z=0
    g15: GeomPoint X=47.0443 Y=-50.4712 Z=0
    g16: Circle CenterX=53.5586 CenterY=-23.2695 CenterZ=0 NormalX=0 NormalY=0 NormalZ=1 AngleXU=0 Radius=3.24518
    g17: Circle CenterX=-195.441 CenterY=-127.082 CenterZ=0 NormalX=0 NormalY=0 NormalZ=1 AngleXU=0 Radius=1
    g18: Circle CenterX=-8.24091 CenterY=-197.481 CenterZ=0 NormalX=0 NormalY=0 NormalZ=1 AngleXU=0 Radius=1
    g19: Circle CenterX=12.8789 CenterY=-141.321 CenterZ=0 NormalX=0 NormalY=0 NormalZ=1 AngleXU=0 Radius=1
    g20: BSplineCurve PolesCount=3 KnotsCount=2 Degree=2 IsPeriodic=0
    g21: GeomPoint X=-195.441 Y=-127.082 Z=0
    g22: GeomPoint X=12.8789 Y=-141.321 Z=0
    g23: Circle CenterX=-12.8016 CenterY=-179.036 CenterZ=0 NormalX=0 NormalY=0 NormalZ=1 AngleXU=0 Radius=10.5072
    g24: Circle CenterX=0.933922 CenterY=-166.43 CenterZ=0 NormalX=0 NormalY=0 NormalZ=1 AngleXU=0 Radius=3.26661
    g25: Circle CenterX=-33.5518 CenterY=-176.44 CenterZ=0 NormalX=0 NormalY=0 NormalZ=1 AngleXU=0 Radius=5.64388
    g26: Circle CenterX=-47.2366 CenterY=-173.859 CenterZ=0 NormalX=0 NormalY=0 NormalZ=1 AngleXU=0 Radius=3.01653
    g27: Circle CenterX=-56.2595 CenterY=-171.456 CenterZ=0 NormalX=0 NormalY=0 NormalZ=1 AngleXU=0 Radius=2.12826
    g28: ArcOfCircle CenterX=51.2151 CenterY=-198.473 CenterZ=0 NormalX=0 NormalY=0 NormalZ=1 AngleXU=0 Radius=20 StartAngle=2.78189 EndAngle=4.35269
    g29: LineSegment StartX=32.4951 StartY=-191.433 StartZ=0 EndX=94.6578 EndY=-26.1352 EndZ=0
    g30: LineSegment StartX=43.1192 StartY=-220.001 StartZ=0 EndX=-196.497 EndY=-129.89 EndZ=0
    g31: LineSegment StartX=43.1192 StartY=-220.001 StartZ=0 EndX=44.1752 EndY=-217.193 EndZ=0
    g32: LineSegment StartX=117.223 StartY=-19.0875 StartZ=0 EndX=117.223 EndY=-16.0875 EndZ=0
    g33: LineSegment StartX=117.223 StartY=-16.0875 StartZ=0 EndX=17.2232 EndY=-16.0875 EndZ=0
    g34: LineSegment StartX=17.2232 StartY=-16.0875 StartZ=0 EndX=17.2232 EndY=-19.0875 EndZ=0
    g35: LineSegment StartX=28.8094 StartY=-19.0875 StartZ=0 EndX=17.2232 EndY=-19.0875 EndZ=0
    g36: LineSegment StartX=47.0443 StartY=-50.4712 StartZ=0 EndX=12.8789 EndY=-141.321 EndZ=0
    g37: LineSegment StartX=-195.441 StartY=-127.082 StartZ=0 EndX=-196.497 EndY=-129.89 EndZ=0
    g38: LineSegment StartX=85.2866 StartY=-36.8766 StartZ=0 EndX=78.9396 EndY=-53.7463 EndZ=0
    g39: LineSegment StartX=60.9579 StartY=-27.7053 StartZ=0 EndX=54.6191 EndY=-44.5532 EndZ=0
    g40: LineSegment StartX=68.0907 StartY=-82.7664 StartZ=0 EndX=61.7465 EndY=-99.6365 EndZ=0
    g41: LineSegment StartX=43.7619 StartY=-73.595 StartZ=0 EndX=37.426 EndY=-90.4435 EndZ=0
    g42: LineSegment StartX=50.885 StartY=-128.652 StartZ=0 EndX=44.5456 EndY=-145.522 EndZ=0
    g43: LineSegment StartX=26.5562 StartY=-119.481 StartZ=0 EndX=20.2251 EndY=-136.329 EndZ=0
    g44: LineSegment StartX=9.3071 StartY=-165.349 StartZ=0 EndX=2.97115 EndY=-182.197 EndZ=0
    g45: LineSegment StartX=33.6358 StartY=-174.52 StartZ=0 EndX=27.2917 EndY=-191.39 EndZ=0
  constraints (71):
    c: Block(g0)
    c: Block(g1)
    c: Block(g2)
    c: Block(g4)
    c: Block(g3)
    c: Block(g6)
    c: Block(g5)
    c: Block(g8)
    c: Block(g7)
    c: Weight(g9) = 1
    c: Equal(g9,g10)
    c: Equal(g9,g11)
    c: Equal(g9,g12)
    c: InternalAlignment(g9-g12 -> g13) x4
    c: InternalAlignment(g14,g13)
    c: InternalAlignment(g15,g13)
    c: Block(g16)
    c: Weight(g17) = 1
    c: Equal(g17,g18)
    c: Equal(g17,g19)
    c: InternalAlignment(g17,g20)
    c: InternalAlignment(g18,g20)
    c: InternalAlignment(g19,g20)
    c: InternalAlignment(g21,g20)
    c: InternalAlignment(g22,g20)
    c: Block(g20)
    c: Block(g23)
    c: Block(g24)
    c: Block(g25)
    c: Block(g26)
    c: Block(g27)
    c: Block(g28)
    c: Coincident(g29,g28)
    c: Coincident(g29,g0)
    c: Block(g13)
    c: Coincident(g31,g30)
    c: Coincident(g31,g28)
    c: Block(g31)
    c: Coincident(g32,g0)
    c: Vertical(g32)
    c: Coincident(g33,g32)
    c: Horizontal(g33)
    c: Coincident(g34,g33)
    c: Vertical(g34)
    c: Block(g33)
    c: Coincident(g35,g13)
    c: Coincident(g35,g34)
    c: Horizontal(g35)
    c: Coincident(g36,g13)
    c: Coincident(g36,g20)
    c: Coincident(g37,g20)
    c: Coincident(g37,g30)
    c: Block(g30)
    c: Coincident(g38,g1)
    c: Coincident(g38,g2)
    c: Coincident(g39,g1)
    c: Coincident(g39,g2)
    c: Coincident(g40,g3)
    c: Coincident(g40,g4)
    c: Coincident(g41,g3)
    c: Coincident(g41,g4)
    c: Coincident(g42,g5)
    c: Coincident(g42,g6)
    c: Coincident(g43,g5)
    c: Coincident(g43,g6)
    c: Coincident(g44,g7)
    c: Coincident(g44,g8)
    c: Coincident(g45,g7)
    c: Coincident(g45,g8)
    c: Distance(g30) = 256
    c: Distance(g33) = 100
FEATURE [Part::Extrusion] Extrude002
  Base = -> Sketch001
  Dir = (1,0,0)
  DirMode = 2
  FaceMakerClass = Part::FaceMakerBullseye
  LengthFwd = 8
  LengthRev = 0
  Solid = true
  Symmetric = false
FEATURE [Sketcher::SketchObject] Sketch002
  FullyConstrained = true
  sketch-geometry (20):
    g0: LineSegment StartX=-2.77179 StartY=-200.304 StartZ=0 EndX=5.22821 EndY=-200.304 EndZ=0
    g1: LineSegment StartX=5.22821 StartY=-200.304 StartZ=0 EndX=5.22821 EndY=-197.304 EndZ=0
    g2: LineSegment StartX=-2.77179 StartY=-200.304 StartZ=0 EndX=-2.77179 EndY=-197.304 EndZ=0
    g3: LineSegment StartX=5.22821 StartY=-197.304 StartZ=0 EndX=8.22821 EndY=-197.304 EndZ=0
    g4: LineSegment StartX=-2.77179 StartY=-197.304 StartZ=0 EndX=-5.77179 EndY=-197.304 EndZ=0
    g5: LineSegment StartX=19.2282 StartY=-203.304 StartZ=0 EndX=19.2282 EndY=-206.304 EndZ=0
    g6: LineSegment StartX=-16.7718 StartY=-203.304 StartZ=0 EndX=-16.7718 EndY=-206.304 EndZ=0
    g7: LineSegment StartX=-16.7718 StartY=-206.304 StartZ=0 EndX=19.2282 EndY=-206.304 EndZ=0
    g8: Circle CenterX=-16.7718 CenterY=-203.304 CenterZ=0 NormalX=0 NormalY=0 NormalZ=1 AngleXU=0 Radius=1
    g9: Circle CenterX=-5.77179 CenterY=-203.304 CenterZ=0 NormalX=0 NormalY=0 NormalZ=1 AngleXU=0 Radius=1
    g10: Circle CenterX=-5.77179 CenterY=-197.304 CenterZ=0 NormalX=0 NormalY=0 NormalZ=1 AngleXU=0 Radius=1
    g11: BSplineCurve PolesCount=3 KnotsCount=2 Degree=2 IsPeriodic=0
    g12: GeomPoint X=-16.7718 Y=-203.304 Z=0
    g13: GeomPoint X=-5.77179 Y=-197.304 Z=0
    g14: Circle CenterX=19.2282 CenterY=-203.304 CenterZ=0 NormalX=0 NormalY=0 NormalZ=1 AngleXU=0 Radius=1
    g15: Circle CenterX=8.22821 CenterY=-203.304 CenterZ=0 NormalX=0 NormalY=0 NormalZ=1 AngleXU=0 Radius=1
    g16: Circle CenterX=8.22821 CenterY=-197.304 CenterZ=0 NormalX=0 NormalY=0 NormalZ=1 AngleXU=0 Radius=1
    g17: BSplineCurve PolesCount=3 KnotsCount=2 Degree=2 IsPeriodic=0
    g18: GeomPoint X=19.2282 Y=-203.304 Z=0
    g19: GeomPoint X=8.22821 Y=-197.304 Z=0
  constraints (41):
    c: Horizontal(g0)
    c: Distance(g0) = 8
    c: Coincident(g1,g0)
    c: Vertical(g1)
    c: Distance(g1) = 3
    c: Coincident(g2,g0)
    c: Vertical(g2)
    c: Distance(g2) = 3
    c: Coincident(g3,g1)
    c: Horizontal(g3)
    c: Distance(g3) = 3
    c: Coincident(g4,g2)
    c: Horizontal(g4)
    c: Distance(g4) = 3
    c: Vertical(g5)
    c: Vertical(g6)
    c: Coincident(g7,g6)
    c: Coincident(g7,g5)
    c: Weight(g8) = 1
    c: Equal(g8,g9)
    c: Equal(g8,g10)
    c: Coincident(g11,g4)
    c: InternalAlignment(g8,g11)
    c: InternalAlignment(g9,g11)
    c: InternalAlignment(g10,g11)
    c: InternalAlignment(g12,g11)
    c: InternalAlignment(g13,g11)
    c: Coincident(g17,g5)
    c: Weight(g14) = 1
    c: Equal(g14,g15)
    c: Equal(g14,g16)
    c: Coincident(g17,g3)
    c: InternalAlignment(g14,g17)
    c: InternalAlignment(g15,g17)
    c: InternalAlignment(g16,g17)
    c: InternalAlignment(g18,g17)
    c: InternalAlignment(g19,g17)
    c: Block(g7)
    c: Block(g17)
    c: Block(g11)
    c: Block(g6)
FEATURE [Part::Extrusion] Extrude003
  Base = -> Sketch002
  Dir = (0,0,1)
  DirMode = 2
  FaceMakerClass = Part::FaceMakerBullseye
  LengthFwd = 260
  LengthRev = 0
  Solid = true
  Symmetric = false
FEATURE [Part::Extrusion] Extrude
  Base = -> Sketch
  Dir = (0,0,1)
  DirMode = 2
  FaceMakerClass = Part::FaceMakerBullseye
  LengthFwd = 14
  LengthRev = 0
  Solid = true
  Symmetric = false
